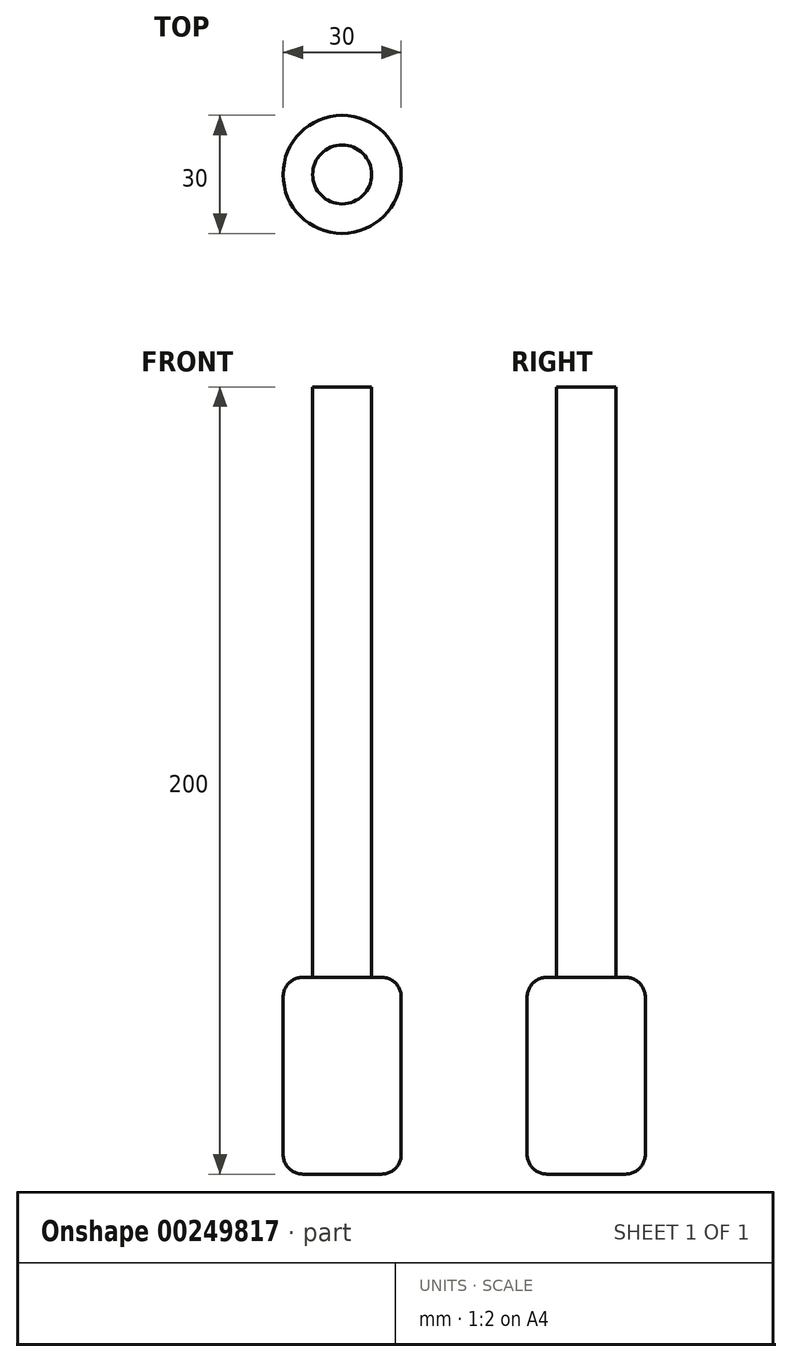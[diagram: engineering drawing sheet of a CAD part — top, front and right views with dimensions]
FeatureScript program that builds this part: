
annotation { "Feature Type Name" : "Feature", "Feature Type Description" : "" }
export const myFeature = defineFeature(function(context is Context, id is Id, definition is map)
    precondition{}
    {
        {
            var Q0;
            Q0=qCreatedBy(makeId("Top.planeOp"),FACE);
            var sketch = newSketch(context, id + "F0", { "sketchPlane" : qUnion([Q0])});
            skCircle(sketch, "E0", {"center": v(0, 0) * mm, "radius": 15 * mm});
            skSolve(sketch);
        }
        {
            var Q0;
            Q0=makeQuery(id+"F0.imprint","IMPRINT",FACE,{"disambiguationData":[TD([[makeQuery(id+"F0.imprint","IMPRINT",EDGE,{"derivedFrom":sQuery(id+"F0.wireOp",EDGE,"E0")}),1.0]])]});
            extrude(context, id + "F1", {"entities" : qUnion([Q0]), "depth" : 50 * mm});
        }
        {
            var Q0;
            Q0=makeQuery(id+"F1.opExtrude","CAP_EDGE",EDGE,{"disambiguationData":[OSD([sQuery(id+"F0.wireOp",EDGE,"E0")])],"isStart":false});
            var Q1;
            Q1=makeQuery(id+"F1.opExtrude","CAP_EDGE",EDGE,{"disambiguationData":[OSD([sQuery(id+"F0.wireOp",EDGE,"E0")])],"isStart":true});
            fillet(context, id + "F2", {"entities" : qUnion([Q0, Q1]), "radius" : 5 * mm, "tangentPropagation" : true, "allowEdgeOverflow" : false});
        }
        {
            var Q0;
            Q0=makeQuery(id+"F1.opExtrude","CAP_FACE",FACE,{"disambiguationData":[OSD([sQuery(id+"F0.wireOp",EDGE,"E0")])],"isStart":false});
            var sketch = newSketch(context, id + "F3", { "sketchPlane" : qUnion([Q0])});
            skCircle(sketch, "E1", {"center": v(0, 0) * mm, "radius": 7.5 * mm});
            skSolve(sketch);
        }
        {
            var Q0;
            Q0 = qSketchRegion(id + "F3", true);
            extrude(context, id + "F4", {"entities" : qUnion([Q0]), "operationType" : NewBodyOperationType.ADD, "depth" : 150 * mm});
        }
    });
